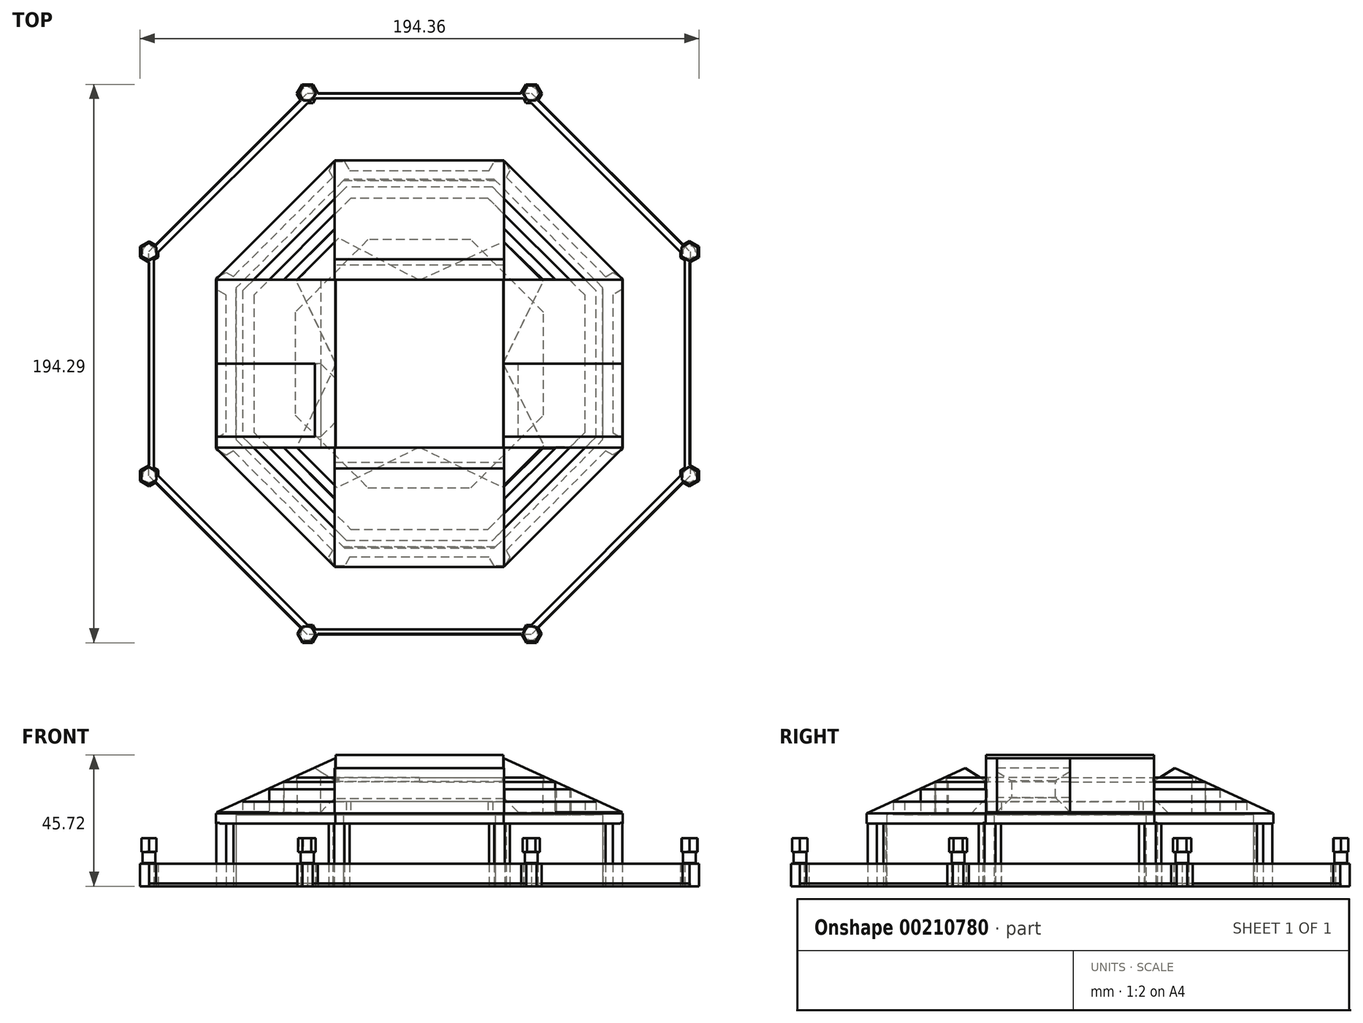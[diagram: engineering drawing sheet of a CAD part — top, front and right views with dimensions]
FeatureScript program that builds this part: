
annotation { "Feature Type Name" : "Feature", "Feature Type Description" : "" }
export const myFeature = defineFeature(function(context is Context, id is Id, definition is map)
    precondition{}
    {
        {
            var Q0;
            Q0=qCreatedBy(makeId("Top.planeOp"),FACE);
            cPlane(context, id + "F0", {"entities" : qUnion([Q0]), "cplaneType" : CPlaneType.OFFSET, "offset" : 31.24 * mm, "width" : 152.4 * mm, "height" : 152.4 * mm});
        }
        {
            var Q0;
            Q0=qCreatedBy(id+"F0.planeOp",FACE);
            cPlane(context, id + "F1", {"entities" : qUnion([Q0]), "cplaneType" : CPlaneType.OFFSET, "offset" : 19.05 * mm, "width" : 152.4 * mm, "height" : 152.4 * mm});
        }
        {
            var Q0;
            Q0=qCreatedBy(id+"F1.planeOp",FACE);
            cPlane(context, id + "F2", {"entities" : qUnion([Q0]), "cplaneType" : CPlaneType.OFFSET, "offset" : 25.4 * mm, "width" : 152.4 * mm, "height" : 152.4 * mm});
        }
        {
            var Q0;
            Q0=qCreatedBy(id+"F2.planeOp",FACE);
            cPlane(context, id + "F3", {"entities" : qUnion([Q0]), "cplaneType" : CPlaneType.OFFSET, "offset" : 6.35 * mm, "width" : 152.4 * mm, "height" : 152.4 * mm});
        }
        {
            var Q0;
            Q0=qCreatedBy(id+"F3.planeOp",FACE);
            cPlane(context, id + "F4", {"entities" : qUnion([Q0]), "cplaneType" : CPlaneType.OFFSET, "offset" : 17.78 * mm, "width" : 152.4 * mm, "height" : 152.4 * mm});
        }
        {
            var Q0;
            Q0=qCreatedBy(id+"F4.planeOp",FACE);
            cPlane(context, id + "F5", {"entities" : qUnion([Q0]), "cplaneType" : CPlaneType.OFFSET, "offset" : 3.3 * mm, "width" : 152.4 * mm, "height" : 152.4 * mm});
        }
        {
            var Q0;
            Q0=qCreatedBy(id+"F5.planeOp",FACE);
            cPlane(context, id + "F6", {"entities" : qUnion([Q0]), "cplaneType" : CPlaneType.OFFSET, "offset" : 34.8 * mm, "width" : 152.4 * mm, "height" : 152.4 * mm});
        }
        {
            var Q0;
            Q0=qCreatedBy(id+"F6.planeOp",FACE);
            var sketch = newSketch(context, id + "F7", { "sketchPlane" : qUnion([Q0])});
            skCircle(sketch, "E0.cCircle", {"center": v(0, 0) * mm, "radius": 94.16 * mm, "construction": true});
            skLineSegment(sketch, "E0.0", {"start": v(94.16, 39) * mm, "end": v(94.16, -39) * mm});
            skLineSegment(sketch, "E0.1", {"start": v(94.16, -39) * mm, "end": v(39, -94.16) * mm});
            skLineSegment(sketch, "E0.2", {"start": v(39, -94.16) * mm, "end": v(-39, -94.16) * mm});
            skLineSegment(sketch, "E0.3", {"start": v(-39, -94.16) * mm, "end": v(-94.16, -39) * mm});
            skLineSegment(sketch, "E0.4", {"start": v(-94.16, -39) * mm, "end": v(-94.16, 39) * mm});
            skLineSegment(sketch, "E0.5", {"start": v(-94.16, 39) * mm, "end": v(-39, 94.16) * mm});
            skLineSegment(sketch, "E0.6", {"start": v(-39, 94.16) * mm, "end": v(39, 94.16) * mm});
            skLineSegment(sketch, "E0.7", {"start": v(39, 94.16) * mm, "end": v(94.16, 39) * mm});
            skPoint(sketch, "E0.0.midPoint", {"position": v(94.16, 0) * mm});
            skCircle(sketch, "E1.cCircle", {"center": v(0, 0) * mm, "radius": 55.27 * mm, "construction": true});
            skLineSegment(sketch, "E1.0", {"start": v(-22.9, 55.27) * mm, "end": v(22.9, 55.27) * mm});
            skLineSegment(sketch, "E1.1", {"start": v(22.9, 55.27) * mm, "end": v(55.27, 22.9) * mm});
            skLineSegment(sketch, "E1.2", {"start": v(55.27, 22.9) * mm, "end": v(55.27, -22.9) * mm});
            skLineSegment(sketch, "E1.3", {"start": v(55.27, -22.9) * mm, "end": v(22.9, -55.27) * mm});
            skLineSegment(sketch, "E1.4", {"start": v(22.9, -55.27) * mm, "end": v(-22.9, -55.27) * mm});
            skLineSegment(sketch, "E1.5", {"start": v(-22.9, -55.27) * mm, "end": v(-55.27, -22.9) * mm});
            skLineSegment(sketch, "E1.6", {"start": v(-55.27, -22.9) * mm, "end": v(-55.27, 22.9) * mm});
            skLineSegment(sketch, "E1.7", {"start": v(-55.27, 22.9) * mm, "end": v(-22.9, 55.27) * mm});
            skPoint(sketch, "E1.0.midPoint", {"position": v(0, 55.27) * mm});
            skSolve(sketch);
        }
        {
            var Q0;
            Q0=qSketchRegion(id+"F7",true);
            extrude(context, id + "F8", {"entities" : qUnion([Q0]), "depth" : 1.02 * mm});
        }
        {
            var Q0;
            Q0=qCreatedBy(id+"F6.planeOp",FACE);
            var sketch = newSketch(context, id + "F9", { "sketchPlane" : qUnion([Q0])});
            skLineSegment(sketch, "E2.0", {"start": v(-38.92, 93.97) * mm, "end": v(38.92, 93.97) * mm});
            skLineSegment(sketch, "E2.1", {"start": v(38.92, 93.97) * mm, "end": v(93.97, 38.92) * mm});
            skLineSegment(sketch, "E2.2", {"start": v(93.97, 38.92) * mm, "end": v(93.97, -38.92) * mm});
            skLineSegment(sketch, "E2.3", {"start": v(93.97, -38.92) * mm, "end": v(38.92, -93.97) * mm});
            skLineSegment(sketch, "E2.4", {"start": v(38.92, -93.97) * mm, "end": v(-38.92, -93.97) * mm});
            skLineSegment(sketch, "E2.5", {"start": v(-38.92, -93.97) * mm, "end": v(-93.97, -38.92) * mm});
            skLineSegment(sketch, "E2.6", {"start": v(-93.97, -38.92) * mm, "end": v(-93.97, 38.92) * mm});
            skLineSegment(sketch, "E2.7", {"start": v(-93.97, 38.92) * mm, "end": v(-38.92, 93.97) * mm});
            skPoint(sketch, "E2.0.midPoint", {"position": v(0, 93.97) * mm});
            skCircle(sketch, "E3.cCircle", {"center": v(-38.92, -93.97) * mm, "radius": 3.1 * mm, "construction": true});
            skLineSegment(sketch, "E3.0", {"start": v(-40.71, -90.87) * mm, "end": v(-37.13, -90.87) * mm});
            skLineSegment(sketch, "E3.1", {"start": v(-37.13, -90.87) * mm, "end": v(-35.34, -93.97) * mm});
            skLineSegment(sketch, "E3.2", {"start": v(-35.34, -93.97) * mm, "end": v(-37.13, -97.07) * mm});
            skLineSegment(sketch, "E3.3", {"start": v(-37.13, -97.07) * mm, "end": v(-40.71, -97.07) * mm});
            skLineSegment(sketch, "E3.4", {"start": v(-40.71, -97.07) * mm, "end": v(-42.5, -93.97) * mm});
            skLineSegment(sketch, "E3.5", {"start": v(-42.5, -93.97) * mm, "end": v(-40.71, -90.87) * mm});
            skPoint(sketch, "E3.0.midPoint", {"position": v(-38.92, -90.87) * mm});
            skCircle(sketch, "E4.cCircle", {"center": v(38.92, -93.97) * mm, "radius": 3.1 * mm, "construction": true});
            skLineSegment(sketch, "E4.0", {"start": v(37.13, -90.87) * mm, "end": v(40.71, -90.87) * mm});
            skLineSegment(sketch, "E4.1", {"start": v(40.71, -90.87) * mm, "end": v(42.5, -93.97) * mm});
            skLineSegment(sketch, "E4.2", {"start": v(42.5, -93.97) * mm, "end": v(40.71, -97.07) * mm});
            skLineSegment(sketch, "E4.3", {"start": v(40.71, -97.07) * mm, "end": v(37.13, -97.07) * mm});
            skLineSegment(sketch, "E4.4", {"start": v(37.13, -97.07) * mm, "end": v(35.34, -93.97) * mm});
            skLineSegment(sketch, "E4.5", {"start": v(35.34, -93.97) * mm, "end": v(37.13, -90.87) * mm});
            skPoint(sketch, "E4.0.midPoint", {"position": v(38.92, -90.87) * mm});
            skCircle(sketch, "E5.cCircle", {"center": v(93.97, -38.92) * mm, "radius": 3.25 * mm, "construction": true});
            skLineSegment(sketch, "E5.0", {"start": v(90.72, -40.8) * mm, "end": v(90.72, -37.05) * mm});
            skLineSegment(sketch, "E5.1", {"start": v(90.72, -37.05) * mm, "end": v(93.97, -35.17) * mm});
            skLineSegment(sketch, "E5.2", {"start": v(93.97, -35.17) * mm, "end": v(97.22, -37.05) * mm});
            skLineSegment(sketch, "E5.3", {"start": v(97.22, -37.05) * mm, "end": v(97.22, -40.8) * mm});
            skLineSegment(sketch, "E5.4", {"start": v(97.22, -40.8) * mm, "end": v(93.97, -42.68) * mm});
            skLineSegment(sketch, "E5.5", {"start": v(93.97, -42.68) * mm, "end": v(90.72, -40.8) * mm});
            skPoint(sketch, "E5.0.midPoint", {"position": v(90.72, -38.92) * mm});
            skCircle(sketch, "E6.cCircle", {"center": v(93.97, 38.92) * mm, "radius": 3.25 * mm, "construction": true});
            skLineSegment(sketch, "E6.0", {"start": v(90.72, 37.05) * mm, "end": v(90.72, 40.8) * mm});
            skLineSegment(sketch, "E6.1", {"start": v(90.72, 40.8) * mm, "end": v(93.97, 42.68) * mm});
            skLineSegment(sketch, "E6.2", {"start": v(93.97, 42.68) * mm, "end": v(97.22, 40.8) * mm});
            skLineSegment(sketch, "E6.3", {"start": v(97.22, 40.8) * mm, "end": v(97.22, 37.05) * mm});
            skLineSegment(sketch, "E6.4", {"start": v(97.22, 37.05) * mm, "end": v(93.97, 35.17) * mm});
            skLineSegment(sketch, "E6.5", {"start": v(93.97, 35.17) * mm, "end": v(90.72, 37.05) * mm});
            skPoint(sketch, "E6.0.midPoint", {"position": v(90.72, 38.92) * mm});
            skCircle(sketch, "E7.cCircle", {"center": v(-93.97, -38.92) * mm, "radius": 3.17 * mm, "construction": true});
            skLineSegment(sketch, "E7.0", {"start": v(-90.8, -37.1) * mm, "end": v(-90.8, -40.76) * mm});
            skLineSegment(sketch, "E7.1", {"start": v(-90.8, -40.76) * mm, "end": v(-93.97, -42.59) * mm});
            skLineSegment(sketch, "E7.2", {"start": v(-93.97, -42.59) * mm, "end": v(-97.14, -40.76) * mm});
            skLineSegment(sketch, "E7.3", {"start": v(-97.14, -40.76) * mm, "end": v(-97.14, -37.1) * mm});
            skLineSegment(sketch, "E7.4", {"start": v(-97.14, -37.1) * mm, "end": v(-93.97, -35.26) * mm});
            skLineSegment(sketch, "E7.5", {"start": v(-93.97, -35.26) * mm, "end": v(-90.8, -37.1) * mm});
            skPoint(sketch, "E7.0.midPoint", {"position": v(-90.8, -38.92) * mm});
            skCircle(sketch, "E8.cCircle", {"center": v(-93.97, 38.92) * mm, "radius": 3.17 * mm, "construction": true});
            skLineSegment(sketch, "E8.0", {"start": v(-90.8, 40.76) * mm, "end": v(-90.8, 37.1) * mm});
            skLineSegment(sketch, "E8.1", {"start": v(-90.8, 37.1) * mm, "end": v(-93.97, 35.26) * mm});
            skLineSegment(sketch, "E8.2", {"start": v(-93.97, 35.26) * mm, "end": v(-97.14, 37.1) * mm});
            skLineSegment(sketch, "E8.3", {"start": v(-97.14, 37.1) * mm, "end": v(-97.14, 40.76) * mm});
            skLineSegment(sketch, "E8.4", {"start": v(-97.14, 40.76) * mm, "end": v(-93.97, 42.59) * mm});
            skLineSegment(sketch, "E8.5", {"start": v(-93.97, 42.59) * mm, "end": v(-90.8, 40.76) * mm});
            skPoint(sketch, "E8.0.midPoint", {"position": v(-90.8, 38.92) * mm});
            skCircle(sketch, "E9.cCircle", {"center": v(-38.92, 93.97) * mm, "radius": 3.25 * mm, "construction": true});
            skLineSegment(sketch, "E9.0", {"start": v(-37.05, 90.72) * mm, "end": v(-40.8, 90.72) * mm});
            skLineSegment(sketch, "E9.1", {"start": v(-40.8, 90.72) * mm, "end": v(-42.67, 93.97) * mm});
            skLineSegment(sketch, "E9.2", {"start": v(-42.67, 93.97) * mm, "end": v(-40.8, 97.22) * mm});
            skLineSegment(sketch, "E9.3", {"start": v(-40.8, 97.22) * mm, "end": v(-37.05, 97.22) * mm});
            skLineSegment(sketch, "E9.4", {"start": v(-37.05, 97.22) * mm, "end": v(-35.18, 93.97) * mm});
            skLineSegment(sketch, "E9.5", {"start": v(-35.18, 93.97) * mm, "end": v(-37.05, 90.72) * mm});
            skPoint(sketch, "E9.0.midPoint", {"position": v(-38.92, 90.72) * mm});
            skCircle(sketch, "E10.cCircle", {"center": v(38.92, 93.97) * mm, "radius": 3.25 * mm, "construction": true});
            skLineSegment(sketch, "E10.0", {"start": v(40.8, 90.72) * mm, "end": v(37.05, 90.72) * mm});
            skLineSegment(sketch, "E10.1", {"start": v(37.05, 90.72) * mm, "end": v(35.18, 93.97) * mm});
            skLineSegment(sketch, "E10.2", {"start": v(35.18, 93.97) * mm, "end": v(37.05, 97.22) * mm});
            skLineSegment(sketch, "E10.3", {"start": v(37.05, 97.22) * mm, "end": v(40.8, 97.22) * mm});
            skLineSegment(sketch, "E10.4", {"start": v(40.8, 97.22) * mm, "end": v(42.67, 93.97) * mm});
            skLineSegment(sketch, "E10.5", {"start": v(42.67, 93.97) * mm, "end": v(40.8, 90.72) * mm});
            skPoint(sketch, "E10.0.midPoint", {"position": v(38.92, 90.72) * mm});
            skLineSegment(sketch, "E11", {"start": v(-36.24, -92.42) * mm, "end": v(36.24, -92.42) * mm});
            skLineSegment(sketch, "E12", {"start": v(92.34, -36.1) * mm, "end": v(92.34, 36.1) * mm});
            skLineSegment(sketch, "E13", {"start": v(36.11, 92.35) * mm, "end": v(-36.11, 92.35) * mm});
            skLineSegment(sketch, "E14", {"start": v(-92.38, 36.17) * mm, "end": v(-92.38, -36.17) * mm});
            skLineSegment(sketch, "E15", {"start": v(38.92, -90.87) * mm, "end": v(90.72, -38.92) * mm});
            skLineSegment(sketch, "E16", {"start": v(90.72, 38.92) * mm, "end": v(38.92, 90.72) * mm});
            skLineSegment(sketch, "E17", {"start": v(-38.92, 90.72) * mm, "end": v(-90.8, 38.92) * mm});
            skLineSegment(sketch, "E18", {"start": v(-90.8, -38.92) * mm, "end": v(-38.92, -90.87) * mm});
            skSolve(sketch);
        }
        {
            var Q0;
            Q0=qSketchRegion(id+"F9",true);
            extrude(context, id + "F10", {"entities" : qUnion([Q0]), "depth" : 7.87 * mm});
        }
        {
            var Q0;
            Q0=qCreatedBy(id+"F6.planeOp",FACE);
            var sketch = newSketch(context, id + "F11", { "sketchPlane" : qUnion([Q0])});
            skLineSegment(sketch, "E19.0", {"start": v(-67.24, -27.85) * mm, "end": v(-67.24, 27.85) * mm});
            skLineSegment(sketch, "E19.1", {"start": v(-67.24, 27.85) * mm, "end": v(-27.85, 67.24) * mm});
            skLineSegment(sketch, "E19.2", {"start": v(-27.85, 67.24) * mm, "end": v(27.85, 67.24) * mm});
            skLineSegment(sketch, "E19.3", {"start": v(27.85, 67.24) * mm, "end": v(67.24, 27.85) * mm});
            skLineSegment(sketch, "E19.4", {"start": v(67.24, 27.85) * mm, "end": v(67.24, -27.85) * mm});
            skLineSegment(sketch, "E19.5", {"start": v(67.24, -27.85) * mm, "end": v(27.85, -67.24) * mm});
            skLineSegment(sketch, "E19.6", {"start": v(27.85, -67.24) * mm, "end": v(-27.85, -67.24) * mm});
            skLineSegment(sketch, "E19.7", {"start": v(-27.85, -67.24) * mm, "end": v(-67.24, -27.85) * mm});
            skPoint(sketch, "E19.0.midPoint", {"position": v(-67.24, 0) * mm});
            skCircle(sketch, "E20.cCircle", {"center": v(67.24, -27.85) * mm, "radius": 3.35 * mm, "construction": true});
            skLineSegment(sketch, "E20.0", {"start": v(70.59, -25.92) * mm, "end": v(70.59, -29.78) * mm});
            skLineSegment(sketch, "E20.1", {"start": v(70.59, -29.78) * mm, "end": v(67.24, -31.72) * mm});
            skLineSegment(sketch, "E20.2", {"start": v(67.24, -31.72) * mm, "end": v(63.89, -29.78) * mm});
            skLineSegment(sketch, "E20.3", {"start": v(63.89, -29.78) * mm, "end": v(63.89, -25.92) * mm});
            skLineSegment(sketch, "E20.4", {"start": v(63.89, -25.92) * mm, "end": v(67.24, -23.98) * mm});
            skLineSegment(sketch, "E20.5", {"start": v(67.24, -23.98) * mm, "end": v(70.59, -25.92) * mm});
            skPoint(sketch, "E20.0.midPoint", {"position": v(70.59, -27.85) * mm});
            skCircle(sketch, "E21.cCircle", {"center": v(67.24, 27.85) * mm, "radius": 3.35 * mm, "construction": true});
            skLineSegment(sketch, "E21.0", {"start": v(70.59, 29.78) * mm, "end": v(70.59, 25.92) * mm});
            skLineSegment(sketch, "E21.1", {"start": v(70.59, 25.92) * mm, "end": v(67.24, 23.98) * mm});
            skLineSegment(sketch, "E21.2", {"start": v(67.24, 23.98) * mm, "end": v(63.89, 25.92) * mm});
            skLineSegment(sketch, "E21.3", {"start": v(63.89, 25.92) * mm, "end": v(63.89, 29.78) * mm});
            skLineSegment(sketch, "E21.4", {"start": v(63.89, 29.78) * mm, "end": v(67.24, 31.72) * mm});
            skLineSegment(sketch, "E21.5", {"start": v(67.24, 31.72) * mm, "end": v(70.59, 29.78) * mm});
            skPoint(sketch, "E21.0.midPoint", {"position": v(70.59, 27.85) * mm});
            skCircle(sketch, "E22.cCircle", {"center": v(27.85, 67.24) * mm, "radius": 3.12 * mm, "construction": true});
            skLineSegment(sketch, "E22.0", {"start": v(26.05, 70.36) * mm, "end": v(29.65, 70.36) * mm});
            skLineSegment(sketch, "E22.1", {"start": v(29.65, 70.36) * mm, "end": v(31.46, 67.24) * mm});
            skLineSegment(sketch, "E22.2", {"start": v(31.46, 67.24) * mm, "end": v(29.65, 64.11) * mm});
            skLineSegment(sketch, "E22.3", {"start": v(29.65, 64.11) * mm, "end": v(26.05, 64.11) * mm});
            skLineSegment(sketch, "E22.4", {"start": v(26.05, 64.11) * mm, "end": v(24.24, 67.24) * mm});
            skLineSegment(sketch, "E22.5", {"start": v(24.24, 67.24) * mm, "end": v(26.05, 70.36) * mm});
            skPoint(sketch, "E22.0.midPoint", {"position": v(27.85, 70.36) * mm});
            skCircle(sketch, "E23.cCircle", {"center": v(-27.85, 67.24) * mm, "radius": 3.12 * mm, "construction": true});
            skLineSegment(sketch, "E23.0", {"start": v(-29.65, 70.36) * mm, "end": v(-26.05, 70.36) * mm});
            skLineSegment(sketch, "E23.1", {"start": v(-26.05, 70.36) * mm, "end": v(-24.24, 67.24) * mm});
            skLineSegment(sketch, "E23.2", {"start": v(-24.24, 67.24) * mm, "end": v(-26.05, 64.11) * mm});
            skLineSegment(sketch, "E23.3", {"start": v(-26.05, 64.11) * mm, "end": v(-29.65, 64.11) * mm});
            skLineSegment(sketch, "E23.4", {"start": v(-29.65, 64.11) * mm, "end": v(-31.46, 67.24) * mm});
            skLineSegment(sketch, "E23.5", {"start": v(-31.46, 67.24) * mm, "end": v(-29.65, 70.36) * mm});
            skPoint(sketch, "E23.0.midPoint", {"position": v(-27.85, 70.36) * mm});
            skCircle(sketch, "E24.cCircle", {"center": v(27.85, -67.24) * mm, "radius": 3.13 * mm, "construction": true});
            skLineSegment(sketch, "E24.0", {"start": v(29.66, -70.37) * mm, "end": v(26.04, -70.37) * mm});
            skLineSegment(sketch, "E24.1", {"start": v(26.04, -70.37) * mm, "end": v(24.23, -67.24) * mm});
            skLineSegment(sketch, "E24.2", {"start": v(24.23, -67.24) * mm, "end": v(26.04, -64.1) * mm});
            skLineSegment(sketch, "E24.3", {"start": v(26.04, -64.1) * mm, "end": v(29.66, -64.1) * mm});
            skLineSegment(sketch, "E24.4", {"start": v(29.66, -64.1) * mm, "end": v(31.47, -67.24) * mm});
            skLineSegment(sketch, "E24.5", {"start": v(31.47, -67.24) * mm, "end": v(29.66, -70.37) * mm});
            skPoint(sketch, "E24.0.midPoint", {"position": v(27.85, -70.37) * mm});
            skCircle(sketch, "E25.cCircle", {"center": v(-27.85, -67.24) * mm, "radius": 3.13 * mm, "construction": true});
            skLineSegment(sketch, "E25.0", {"start": v(-26.04, -70.37) * mm, "end": v(-29.66, -70.37) * mm});
            skLineSegment(sketch, "E25.1", {"start": v(-29.66, -70.37) * mm, "end": v(-31.47, -67.24) * mm});
            skLineSegment(sketch, "E25.2", {"start": v(-31.47, -67.24) * mm, "end": v(-29.66, -64.1) * mm});
            skLineSegment(sketch, "E25.3", {"start": v(-29.66, -64.1) * mm, "end": v(-26.04, -64.1) * mm});
            skLineSegment(sketch, "E25.4", {"start": v(-26.04, -64.1) * mm, "end": v(-24.23, -67.24) * mm});
            skLineSegment(sketch, "E25.5", {"start": v(-24.23, -67.24) * mm, "end": v(-26.04, -70.37) * mm});
            skPoint(sketch, "E25.0.midPoint", {"position": v(-27.85, -70.37) * mm});
            skCircle(sketch, "E26.cCircle", {"center": v(-67.24, -27.85) * mm, "radius": 3.44 * mm, "construction": true});
            skLineSegment(sketch, "E26.0", {"start": v(-70.68, -29.84) * mm, "end": v(-70.68, -25.86) * mm});
            skLineSegment(sketch, "E26.1", {"start": v(-70.68, -25.86) * mm, "end": v(-67.24, -23.88) * mm});
            skLineSegment(sketch, "E26.2", {"start": v(-67.24, -23.88) * mm, "end": v(-63.8, -25.86) * mm});
            skLineSegment(sketch, "E26.3", {"start": v(-63.8, -25.86) * mm, "end": v(-63.8, -29.84) * mm});
            skLineSegment(sketch, "E26.4", {"start": v(-63.8, -29.84) * mm, "end": v(-67.24, -31.82) * mm});
            skLineSegment(sketch, "E26.5", {"start": v(-67.24, -31.82) * mm, "end": v(-70.68, -29.84) * mm});
            skPoint(sketch, "E26.0.midPoint", {"position": v(-70.68, -27.85) * mm});
            skCircle(sketch, "E27.cCircle", {"center": v(-67.24, 27.85) * mm, "radius": 3.44 * mm, "construction": true});
            skLineSegment(sketch, "E27.0", {"start": v(-70.68, 25.86) * mm, "end": v(-70.68, 29.84) * mm});
            skLineSegment(sketch, "E27.1", {"start": v(-70.68, 29.84) * mm, "end": v(-67.24, 31.82) * mm});
            skLineSegment(sketch, "E27.2", {"start": v(-67.24, 31.82) * mm, "end": v(-63.8, 29.84) * mm});
            skLineSegment(sketch, "E27.3", {"start": v(-63.8, 29.84) * mm, "end": v(-63.8, 25.86) * mm});
            skLineSegment(sketch, "E27.4", {"start": v(-63.8, 25.86) * mm, "end": v(-67.24, 23.88) * mm});
            skLineSegment(sketch, "E27.5", {"start": v(-67.24, 23.88) * mm, "end": v(-70.68, 25.86) * mm});
            skPoint(sketch, "E27.0.midPoint", {"position": v(-70.68, 27.85) * mm});
            skLineSegment(sketch, "E28", {"start": v(-26.04, -64.1) * mm, "end": v(26.04, -64.1) * mm});
            skLineSegment(sketch, "E29", {"start": v(26.04, -64.1) * mm, "end": v(63.89, -25.92) * mm});
            skLineSegment(sketch, "E30", {"start": v(63.89, -25.92) * mm, "end": v(63.89, 25.92) * mm});
            skLineSegment(sketch, "E31", {"start": v(63.89, 25.92) * mm, "end": v(26.05, 64.11) * mm});
            skLineSegment(sketch, "E32", {"start": v(26.05, 64.11) * mm, "end": v(-26.05, 64.11) * mm});
            skLineSegment(sketch, "E33", {"start": v(-26.05, 64.11) * mm, "end": v(-63.8, 25.86) * mm});
            skLineSegment(sketch, "E34", {"start": v(-63.8, 25.86) * mm, "end": v(-63.8, -25.86) * mm});
            skLineSegment(sketch, "E35", {"start": v(-63.8, -25.86) * mm, "end": v(-26.04, -64.1) * mm});
            skSolve(sketch);
        }
        {
            var Q0;
            Q0=qSketchRegion(id+"F11",true);
            extrude(context, id + "F12", {"entities" : qUnion([Q0]), "depth" : 22.1 * mm});
        }
        {
            var Q0;
            Q0=qCreatedBy(id+"F6.planeOp",FACE);
            cPlane(context, id + "F13", {"entities" : qUnion([Q0]), "cplaneType" : CPlaneType.OFFSET, "offset" : 21.84 * mm, "width" : 152.4 * mm, "height" : 152.4 * mm});
        }
        {
            var Q0;
            Q0=qCreatedBy(id+"F13.planeOp",FACE);
            var sketch = newSketch(context, id + "F14", { "sketchPlane" : qUnion([Q0])});
            skCircle(sketch, "E36.cCircle", {"center": v(0, 0) * mm, "radius": 70.74 * mm, "construction": true});
            skLineSegment(sketch, "E36.0", {"start": v(29.3, -70.74) * mm, "end": v(-29.3, -70.74) * mm});
            skLineSegment(sketch, "E36.1", {"start": v(-29.3, -70.74) * mm, "end": v(-70.74, -29.3) * mm});
            skLineSegment(sketch, "E36.2", {"start": v(-70.74, -29.3) * mm, "end": v(-70.74, 29.3) * mm});
            skLineSegment(sketch, "E36.3", {"start": v(-70.74, 29.3) * mm, "end": v(-29.3, 70.74) * mm});
            skLineSegment(sketch, "E36.4", {"start": v(-29.3, 70.74) * mm, "end": v(29.3, 70.74) * mm});
            skLineSegment(sketch, "E36.5", {"start": v(29.3, 70.74) * mm, "end": v(70.74, 29.3) * mm});
            skLineSegment(sketch, "E36.6", {"start": v(70.74, 29.3) * mm, "end": v(70.74, -29.3) * mm});
            skLineSegment(sketch, "E36.7", {"start": v(70.74, -29.3) * mm, "end": v(29.3, -70.74) * mm});
            skPoint(sketch, "E36.0.midPoint", {"position": v(0, -70.74) * mm});
            skCircle(sketch, "E37.cCircle", {"center": v(0, 0) * mm, "radius": 43.18 * mm, "construction": true});
            skLineSegment(sketch, "E37.0", {"start": v(17.89, -43.18) * mm, "end": v(-17.89, -43.18) * mm});
            skLineSegment(sketch, "E37.1", {"start": v(-17.89, -43.18) * mm, "end": v(-43.18, -17.89) * mm});
            skLineSegment(sketch, "E37.2", {"start": v(-43.18, -17.89) * mm, "end": v(-43.18, 17.89) * mm});
            skLineSegment(sketch, "E37.3", {"start": v(-43.18, 17.89) * mm, "end": v(-17.89, 43.18) * mm});
            skLineSegment(sketch, "E37.4", {"start": v(-17.89, 43.18) * mm, "end": v(17.89, 43.18) * mm});
            skLineSegment(sketch, "E37.5", {"start": v(17.89, 43.18) * mm, "end": v(43.18, 17.89) * mm});
            skLineSegment(sketch, "E37.6", {"start": v(43.18, 17.89) * mm, "end": v(43.18, -17.89) * mm});
            skLineSegment(sketch, "E37.7", {"start": v(43.18, -17.89) * mm, "end": v(17.89, -43.18) * mm});
            skPoint(sketch, "E37.0.midPoint", {"position": v(0, -43.18) * mm});
            skSolve(sketch);
        }
        {
            var Q0;
            Q0=qSketchRegion(id+"F14",true);
            extrude(context, id + "F15", {"entities" : qUnion([Q0]), "operationType" : NewBodyOperationType.ADD, "depth" : 3.56 * mm});
        }
        {
            var Q0;
            Q0=qCreatedBy(makeId("Front.planeOp"),FACE);
            var sketch = newSketch(context, id + "F16", { "sketchPlane" : qUnion([Q0])});
            skPoint(sketch, "E38.0.midPoint", {"position": v(0, 189.03) * mm});
            skLineSegment(sketch, "E39.left", {"start": v(-70.52, 163.7) * mm, "end": v(-70.52, 163.7) * mm});
            skLineSegment(sketch, "E39.right", {"start": v(70.52, 163.7) * mm, "end": v(70.52, 163.7) * mm});
            skPoint(sketch, "E39.middle", {"position": v(0, 163.7) * mm});
            skLineSegment(sketch, "E40", {"start": v(-29.24, 163.7) * mm, "end": v(-29.24, 182.4) * mm});
            skLineSegment(sketch, "E41", {"start": v(-29.24, 182.4) * mm, "end": v(-70.52, 163.7) * mm});
            skLineSegment(sketch, "E42", {"start": v(29.24, 182.4) * mm, "end": v(70.52, 163.7) * mm});
            skLineSegment(sketch, "E43", {"start": v(29.24, 182.4) * mm, "end": v(29.24, 163.7) * mm});
            skLineSegment(sketch, "E44", {"start": v(29.24, 163.7) * mm, "end": v(70.52, 163.7) * mm});
            skLineSegment(sketch, "E45", {"start": v(-70.52, 163.7) * mm, "end": v(-29.24, 163.7) * mm});
            skSolve(sketch);
        }
        {
            var Q0;
            Q0=qSketchRegion(id+"F16",true);
            extrude(context, id + "F17", {"entities" : qUnion([Q0]), "endBound" : BoundingType.SYMMETRIC, "depth" : 58.42 * mm});
        }
        {
            var Q0;
            Q0=qCreatedBy(makeId("Right.planeOp"),FACE);
            var sketch = newSketch(context, id + "F18", { "sketchPlane" : qUnion([Q0])});
            skPoint(sketch, "E46.0.midPoint", {"position": v(0, 188.96) * mm});
            skLineSegment(sketch, "E47.bottom", {"start": v(70.71, 163.3) * mm, "end": v(-70.71, 163.3) * mm});
            skLineSegment(sketch, "E47.top", {"start": v(70.71, 163.3) * mm, "end": v(-70.71, 163.3) * mm});
            skLineSegment(sketch, "E47.left", {"start": v(70.71, 163.3) * mm, "end": v(70.71, 163.3) * mm});
            skLineSegment(sketch, "E47.right", {"start": v(-70.71, 163.3) * mm, "end": v(-70.71, 163.3) * mm});
            skPoint(sketch, "E47.middle", {"position": v(0, 163.3) * mm});
            skLineSegment(sketch, "E48", {"start": v(-29.2, 182.35) * mm, "end": v(-29.2, 163.3) * mm});
            skLineSegment(sketch, "E49", {"start": v(29.2, 182.35) * mm, "end": v(29.2, 163.3) * mm});
            skLineSegment(sketch, "E50", {"start": v(-70.71, 163.3) * mm, "end": v(-29.2, 163.3) * mm});
            skLineSegment(sketch, "E51", {"start": v(-70.71, 163.3) * mm, "end": v(-29.2, 182.35) * mm});
            skLineSegment(sketch, "E52", {"start": v(29.2, 182.35) * mm, "end": v(70.71, 163.3) * mm});
            skSolve(sketch);
        }
        {
            var Q0;
            Q0=qSketchRegion(id+"F18",true);
            extrude(context, id + "F19", {"entities" : qUnion([Q0]), "endBound" : BoundingType.SYMMETRIC, "depth" : 58.93 * mm});
        }
        {
            var Q0;
            Q0=qSketchRegion(id+"F16",true);
            extrude(context, id + "F20", {"entities" : qUnion([Q0]), "depth" : 25.4 * mm});
        }
        {
            var Q0;
            Q0=qCreatedBy(id+"F13.planeOp",FACE);
            var sketch = newSketch(context, id + "F21", { "sketchPlane" : qUnion([Q0])});
            skCircle(sketch, "E53.cCircle", {"center": v(0, 0) * mm, "radius": 57.6 * mm, "construction": true});
            skLineSegment(sketch, "E53.0", {"start": v(57.6, 23.86) * mm, "end": v(57.6, -23.86) * mm});
            skLineSegment(sketch, "E53.1", {"start": v(57.6, -23.86) * mm, "end": v(23.86, -57.6) * mm});
            skLineSegment(sketch, "E53.2", {"start": v(23.86, -57.6) * mm, "end": v(-23.86, -57.6) * mm});
            skLineSegment(sketch, "E53.3", {"start": v(-23.86, -57.6) * mm, "end": v(-57.6, -23.86) * mm});
            skLineSegment(sketch, "E53.4", {"start": v(-57.6, -23.86) * mm, "end": v(-57.6, 23.86) * mm});
            skLineSegment(sketch, "E53.5", {"start": v(-57.6, 23.86) * mm, "end": v(-23.86, 57.6) * mm});
            skLineSegment(sketch, "E53.6", {"start": v(-23.86, 57.6) * mm, "end": v(23.86, 57.6) * mm});
            skLineSegment(sketch, "E53.7", {"start": v(23.86, 57.6) * mm, "end": v(57.6, 23.86) * mm});
            skPoint(sketch, "E53.0.midPoint", {"position": v(57.6, 0) * mm});
            skCircle(sketch, "E54.cCircle", {"center": v(0, 0) * mm, "radius": 61.43 * mm, "construction": true});
            skPoint(sketch, "E54.cCircle.perimeterSnap0", {"position": v(-57.6, 0) * mm});
            skLineSegment(sketch, "E54.0", {"start": v(-61.43, -25.45) * mm, "end": v(-61.43, 25.45) * mm});
            skLineSegment(sketch, "E54.1", {"start": v(-61.43, 25.45) * mm, "end": v(-25.45, 61.43) * mm});
            skLineSegment(sketch, "E54.2", {"start": v(-25.45, 61.43) * mm, "end": v(25.45, 61.43) * mm});
            skLineSegment(sketch, "E54.3", {"start": v(25.45, 61.43) * mm, "end": v(61.43, 25.45) * mm});
            skLineSegment(sketch, "E54.4", {"start": v(61.43, 25.45) * mm, "end": v(61.43, -25.45) * mm});
            skLineSegment(sketch, "E54.5", {"start": v(61.43, -25.45) * mm, "end": v(25.45, -61.43) * mm});
            skLineSegment(sketch, "E54.6", {"start": v(25.45, -61.43) * mm, "end": v(-25.45, -61.43) * mm});
            skLineSegment(sketch, "E54.7", {"start": v(-25.45, -61.43) * mm, "end": v(-61.43, -25.45) * mm});
            skPoint(sketch, "E54.0.midPoint", {"position": v(-61.43, 0) * mm});
            skPoint(sketch, "E54.0.midPoint.positionSnap0", {"position": v(-57.6, 0) * mm});
            skSolve(sketch);
        }
        {
            var Q0;
            Q0=qSketchRegion(id+"F21",true);
            extrude(context, id + "F22", {"entities" : qUnion([Q0]), "depth" : 7.62 * mm});
        }
        {
            var Q0;
            Q0=qCreatedBy(id+"F13.planeOp",FACE);
            var sketch = newSketch(context, id + "F23", { "sketchPlane" : qUnion([Q0])});
            skPoint(sketch, "E55.0.midPoint", {"position": v(-40.84, 40.66) * mm});
            skPoint(sketch, "E56.0.midPoint", {"position": v(0, 54.02) * mm});
            skLineSegment(sketch, "E57", {"start": v(52.63, -28.82) * mm, "end": v(47.58, -28.82) * mm});
            skLineSegment(sketch, "E58", {"start": v(29.57, -51.99) * mm, "end": v(29.57, -46.84) * mm});
            skLineSegment(sketch, "E59", {"start": v(52.3, 29.26) * mm, "end": v(47.14, 29.26) * mm});
            skLineSegment(sketch, "E60", {"start": v(47.14, 29.26) * mm, "end": v(52.3, 29.26) * mm});
            skLineSegment(sketch, "E61", {"start": v(29.46, 52) * mm, "end": v(29.46, 46.95) * mm});
            skLineSegment(sketch, "E62", {"start": v(-29.43, 46.97) * mm, "end": v(-29.43, 52.13) * mm});
            skLineSegment(sketch, "E63", {"start": v(-47.2, 29.2) * mm, "end": v(-52.24, 29.2) * mm});
            skLineSegment(sketch, "E64", {"start": v(-52.24, 29.2) * mm, "end": v(-47.2, 29.2) * mm});
            skLineSegment(sketch, "E65", {"start": v(-47.2, -29.2) * mm, "end": v(-52.24, -29.2) * mm});
            skLineSegment(sketch, "E66", {"start": v(-29.46, -46.94) * mm, "end": v(-29.46, -52) * mm});
            skLineSegment(sketch, "E67", {"start": v(-29.46, -52) * mm, "end": v(-29.46, -45.28) * mm});
            skLineSegment(sketch, "E68", {"start": v(29.57, -51.99) * mm, "end": v(52.63, -28.82) * mm});
            skLineSegment(sketch, "E69", {"start": v(47.58, -28.82) * mm, "end": v(29.57, -46.84) * mm});
            skLineSegment(sketch, "E70", {"start": v(47.14, 29.26) * mm, "end": v(29.46, 46.95) * mm});
            skLineSegment(sketch, "E71", {"start": v(52.3, 29.26) * mm, "end": v(29.46, 52) * mm});
            skLineSegment(sketch, "E72", {"start": v(29.46, 46.95) * mm, "end": v(47.14, 29.26) * mm});
            skLineSegment(sketch, "E73", {"start": v(-52.24, 29.2) * mm, "end": v(-29.43, 52.13) * mm});
            skLineSegment(sketch, "E74", {"start": v(-29.43, 46.97) * mm, "end": v(-47.2, 29.2) * mm});
            skLineSegment(sketch, "E75", {"start": v(-52.24, -29.2) * mm, "end": v(-29.46, -52) * mm});
            skLineSegment(sketch, "E76", {"start": v(-47.2, -29.2) * mm, "end": v(-29.46, -46.94) * mm});
            skSolve(sketch);
        }
        {
            var Q0;
            Q0=qSketchRegion(id+"F23",true);
            extrude(context, id + "F24", {"entities" : qUnion([Q0]), "depth" : 11.94 * mm});
        }
        {
            var Q0;
            Q0=qCreatedBy(id+"F13.planeOp",FACE);
            var sketch = newSketch(context, id + "F25", { "sketchPlane" : qUnion([Q0])});
            skLineSegment(sketch, "E77", {"start": v(-47.23, 29.16) * mm, "end": v(-29.4, 46.93) * mm});
            skLineSegment(sketch, "E78", {"start": v(-29.4, 46.93) * mm, "end": v(-29.4, 42.28) * mm});
            skLineSegment(sketch, "E79", {"start": v(-29.4, 42.28) * mm, "end": v(-42.6, 29.16) * mm});
            skLineSegment(sketch, "E80", {"start": v(-47.23, 29.16) * mm, "end": v(-42.6, 29.16) * mm});
            skLineSegment(sketch, "E81", {"start": v(-47.23, -29.1) * mm, "end": v(-42.6, -29.1) * mm});
            skLineSegment(sketch, "E82", {"start": v(-42.6, -29.1) * mm, "end": v(-29.4, -42.37) * mm});
            skLineSegment(sketch, "E83", {"start": v(-29.4, -42.37) * mm, "end": v(-29.4, -46.79) * mm});
            skLineSegment(sketch, "E84", {"start": v(-29.4, -46.79) * mm, "end": v(-47.23, -29.1) * mm});
            skLineSegment(sketch, "E85", {"start": v(29.45, 47.07) * mm, "end": v(47.17, 29.34) * mm});
            skLineSegment(sketch, "E86", {"start": v(29.45, 42.28) * mm, "end": v(42.87, 29.34) * mm});
            skLineSegment(sketch, "E87", {"start": v(29.45, 47.07) * mm, "end": v(29.45, 42.28) * mm});
            skLineSegment(sketch, "E88", {"start": v(42.87, 29.34) * mm, "end": v(47.17, 29.34) * mm});
            skLineSegment(sketch, "E89", {"start": v(47.17, -29.43) * mm, "end": v(29.45, -47.13) * mm});
            skLineSegment(sketch, "E90", {"start": v(42.87, -29.43) * mm, "end": v(29.45, -42.83) * mm});
            skLineSegment(sketch, "E91", {"start": v(42.87, -29.43) * mm, "end": v(47.17, -29.43) * mm});
            skLineSegment(sketch, "E92", {"start": v(29.45, -42.83) * mm, "end": v(29.45, -47.13) * mm});
            skSolve(sketch);
        }
        {
            var Q0;
            Q0=qSketchRegion(id+"F25",true);
            extrude(context, id + "F26", {"entities" : qUnion([Q0]), "depth" : 14.48 * mm});
        }
        {
            var Q0;
            Q0=qCreatedBy(id+"F13.planeOp",FACE);
            cPlane(context, id + "F27", {"entities" : qUnion([Q0]), "cplaneType" : CPlaneType.OFFSET, "offset" : 14.48 * mm, "width" : 152.4 * mm, "height" : 152.4 * mm});
        }
        {
            var Q0;
            Q0=qCreatedBy(id+"F27.planeOp",FACE);
            var sketch = newSketch(context, id + "F28", { "sketchPlane" : qUnion([Q0])});
            skPoint(sketch, "E93.0.midPoint", {"position": v(-35.87, 35.88) * mm});
            skPoint(sketch, "E94.0.midPoint", {"position": v(0, 29.06) * mm});
            skLineSegment(sketch, "E95", {"start": v(0, 29.06) * mm, "end": v(-28.05, 43.7) * mm});
            skLineSegment(sketch, "E96", {"start": v(0, 29.06) * mm, "end": v(29.23, 42.52) * mm});
            skLineSegment(sketch, "E97", {"start": v(29.06, 0) * mm, "end": v(43.03, 28.71) * mm});
            skLineSegment(sketch, "E98", {"start": v(-29.06, 0) * mm, "end": v(-42.84, 28.91) * mm});
            skLineSegment(sketch, "E99", {"start": v(-29.06, 0) * mm, "end": v(-42.7, -29.05) * mm});
            skLineSegment(sketch, "E100", {"start": v(0, -29.06) * mm, "end": v(-28.62, -43.13) * mm});
            skLineSegment(sketch, "E101", {"start": v(0, -29.06) * mm, "end": v(28.84, -42.9) * mm});
            skLineSegment(sketch, "E102", {"start": v(29.06, 0) * mm, "end": v(43.29, -28.46) * mm});
            skLineSegment(sketch, "E103", {"start": v(-42.7, -29.05) * mm, "end": v(-28.62, -43.13) * mm});
            skLineSegment(sketch, "E104", {"start": v(28.84, -42.9) * mm, "end": v(43.29, -28.46) * mm});
            skLineSegment(sketch, "E105", {"start": v(43.03, 28.71) * mm, "end": v(29.23, 42.52) * mm});
            skLineSegment(sketch, "E106", {"start": v(-28.05, 43.7) * mm, "end": v(-42.84, 28.91) * mm});
            skSolve(sketch);
        }
        {
            var Q0;
            Q0=qSketchRegion(id+"F28",true);
            extrude(context, id + "F29", {"entities" : qUnion([Q0]), "depth" : 1.52 * mm});
        }
        {
            var Q0;
            Q0=qCreatedBy(id+"F27.planeOp",FACE);
            cPlane(context, id + "F30", {"entities" : qUnion([Q0]), "cplaneType" : CPlaneType.OFFSET, "offset" : 1.52 * mm, "width" : 152.4 * mm, "height" : 152.4 * mm});
        }
        {
            var Q0;
            Q0=qCreatedBy(id+"F30.planeOp",FACE);
            var sketch = newSketch(context, id + "F31", { "sketchPlane" : qUnion([Q0])});
            skLineSegment(sketch, "E107.bottom", {"start": v(-29.15, 29.2) * mm, "end": v(29.15, 29.2) * mm});
            skLineSegment(sketch, "E107.top", {"start": v(-29.15, -29.2) * mm, "end": v(29.15, -29.2) * mm});
            skLineSegment(sketch, "E107.left", {"start": v(-29.15, 29.2) * mm, "end": v(-29.15, -29.2) * mm});
            skLineSegment(sketch, "E107.right", {"start": v(29.15, 29.2) * mm, "end": v(29.15, -29.2) * mm});
            skPoint(sketch, "E107.middle", {"position": v(0, 0) * mm});
            skSolve(sketch);
        }
        {
            var Q0;
            Q0=qSketchRegion(id+"F31",true);
            extrude(context, id + "F32", {"entities" : qUnion([Q0]), "depth" : 7.87 * mm});
        }
        {
            var Q0;
            Q0=makeQuery(id+"F8.opExtrude","CAP_FACE",FACE,{"disambiguationData":[OSD([sQuery(id+"F7.wireOp",EDGE,"E0.0"),sQuery(id+"F7.wireOp",EDGE,"E0.1"),sQuery(id+"F7.wireOp",EDGE,"E0.2"),sQuery(id+"F7.wireOp",EDGE,"E0.3"),sQuery(id+"F7.wireOp",EDGE,"E0.4"),sQuery(id+"F7.wireOp",EDGE,"E0.5"),sQuery(id+"F7.wireOp",EDGE,"E0.6"),sQuery(id+"F7.wireOp",EDGE,"E0.7"),sQuery(id+"F7.wireOp",EDGE,"E1.0"),sQuery(id+"F7.wireOp",EDGE,"E1.1"),sQuery(id+"F7.wireOp",EDGE,"E1.2"),sQuery(id+"F7.wireOp",EDGE,"E1.3"),sQuery(id+"F7.wireOp",EDGE,"E1.4"),sQuery(id+"F7.wireOp",EDGE,"E1.5"),sQuery(id+"F7.wireOp",EDGE,"E1.6"),sQuery(id+"F7.wireOp",EDGE,"E1.7")])],"isStart":true});
            var sketch = newSketch(context, id + "F33", { "sketchPlane" : qUnion([Q0])});
            skCircle(sketch, "E108.cCircle", {"center": v(0, 0) * mm, "radius": 63.77 * mm, "construction": true});
            skPoint(sketch, "E108.cCircle.perimeterSnap0", {"position": v(0, 55.27) * mm});
            skLineSegment(sketch, "E108.0", {"start": v(-26.41, 63.77) * mm, "end": v(26.41, 63.77) * mm});
            skLineSegment(sketch, "E108.1", {"start": v(26.41, 63.77) * mm, "end": v(63.77, 26.41) * mm});
            skLineSegment(sketch, "E108.2", {"start": v(63.77, 26.41) * mm, "end": v(63.77, -26.41) * mm});
            skLineSegment(sketch, "E108.3", {"start": v(63.77, -26.41) * mm, "end": v(26.41, -63.77) * mm});
            skLineSegment(sketch, "E108.4", {"start": v(26.41, -63.77) * mm, "end": v(-26.41, -63.77) * mm});
            skLineSegment(sketch, "E108.5", {"start": v(-26.41, -63.77) * mm, "end": v(-63.77, -26.41) * mm});
            skLineSegment(sketch, "E108.6", {"start": v(-63.77, -26.41) * mm, "end": v(-63.77, 26.41) * mm});
            skLineSegment(sketch, "E108.7", {"start": v(-63.77, 26.41) * mm, "end": v(-26.41, 63.77) * mm});
            skPoint(sketch, "E108.0.midPoint", {"position": v(0, 63.77) * mm});
            skPoint(sketch, "E108.0.midPoint.positionSnap0", {"position": v(0, 55.27) * mm});
            skSolve(sketch);
        }
        {
            var Q0;
            Q0 = qSketchRegion(id + "F33", true);
            extrude(context, id + "F34", {"entities" : qUnion([Q0]), "operationType" : NewBodyOperationType.REMOVE, "oppositeDirection" : true, "depth" : 24.9 * mm});
        }
        {
            var Q0;
            Q0=qCreatedBy(id+"F13.planeOp",FACE);
            var sketch = newSketch(context, id + "F35", { "sketchPlane" : qUnion([Q0])});
            skCircle(sketch, "E109.cCircle", {"center": v(0, 0) * mm, "radius": 63.65 * mm, "construction": true});
            skLineSegment(sketch, "E109.0", {"start": v(63.65, 26.37) * mm, "end": v(63.65, -26.37) * mm});
            skLineSegment(sketch, "E109.1", {"start": v(63.65, -26.37) * mm, "end": v(26.37, -63.65) * mm});
            skLineSegment(sketch, "E109.2", {"start": v(26.37, -63.65) * mm, "end": v(-26.37, -63.65) * mm});
            skLineSegment(sketch, "E109.3", {"start": v(-26.37, -63.65) * mm, "end": v(-63.65, -26.37) * mm});
            skLineSegment(sketch, "E109.4", {"start": v(-63.65, -26.37) * mm, "end": v(-63.65, 26.37) * mm});
            skLineSegment(sketch, "E109.5", {"start": v(-63.65, 26.37) * mm, "end": v(-26.37, 63.65) * mm});
            skLineSegment(sketch, "E109.6", {"start": v(-26.37, 63.65) * mm, "end": v(26.37, 63.65) * mm});
            skLineSegment(sketch, "E109.7", {"start": v(26.37, 63.65) * mm, "end": v(63.65, 26.37) * mm});
            skPoint(sketch, "E109.0.midPoint", {"position": v(63.65, 0) * mm});
            skSolve(sketch);
        }
        {
            var Q0;
            Q0 = qSketchRegion(id + "F35", true);
            extrude(context, id + "F36", {"entities" : qUnion([Q0]), "operationType" : NewBodyOperationType.REMOVE, "oppositeDirection" : true, "depth" : 86.36 * mm});
        }
        {
            var Q0;
            Q0=makeQuery(id+"F15.boolean.opBoolean","INTERSECT",EDGE,{"derivedFrom":[makeQuery(id+"F12.opExtrude","SWEPT_FACE",FACE,{"disambiguationData":[OSD([sQuery(id+"F11.wireOp",EDGE,"E33")])]}),makeQuery(id+"F15.opExtrude","CAP_FACE",FACE,{"disambiguationData":[OSD([sQuery(id+"F14.wireOp",EDGE,"E36.0"),sQuery(id+"F14.wireOp",EDGE,"E36.1"),sQuery(id+"F14.wireOp",EDGE,"E36.2"),sQuery(id+"F14.wireOp",EDGE,"E36.3"),sQuery(id+"F14.wireOp",EDGE,"E36.4"),sQuery(id+"F14.wireOp",EDGE,"E36.5"),sQuery(id+"F14.wireOp",EDGE,"E36.6"),sQuery(id+"F14.wireOp",EDGE,"E36.7"),sQuery(id+"F14.wireOp",EDGE,"E37.0"),sQuery(id+"F14.wireOp",EDGE,"E37.1"),sQuery(id+"F14.wireOp",EDGE,"E37.2"),sQuery(id+"F14.wireOp",EDGE,"E37.3"),sQuery(id+"F14.wireOp",EDGE,"E37.4"),sQuery(id+"F14.wireOp",EDGE,"E37.5"),sQuery(id+"F14.wireOp",EDGE,"E37.6"),sQuery(id+"F14.wireOp",EDGE,"E37.7")])],"isStart":true})]});
            var Q1;
            Q1=makeQuery(id+"F15.boolean.opBoolean","INTERSECT",EDGE,{"derivedFrom":[makeQuery(id+"F12.opExtrude","SWEPT_FACE",FACE,{"disambiguationData":[OSD([sQuery(id+"F11.wireOp",EDGE,"E32")])]}),makeQuery(id+"F15.opExtrude","CAP_FACE",FACE,{"disambiguationData":[OSD([sQuery(id+"F14.wireOp",EDGE,"E36.0"),sQuery(id+"F14.wireOp",EDGE,"E36.1"),sQuery(id+"F14.wireOp",EDGE,"E36.2"),sQuery(id+"F14.wireOp",EDGE,"E36.3"),sQuery(id+"F14.wireOp",EDGE,"E36.4"),sQuery(id+"F14.wireOp",EDGE,"E36.5"),sQuery(id+"F14.wireOp",EDGE,"E36.6"),sQuery(id+"F14.wireOp",EDGE,"E36.7"),sQuery(id+"F14.wireOp",EDGE,"E37.0"),sQuery(id+"F14.wireOp",EDGE,"E37.1"),sQuery(id+"F14.wireOp",EDGE,"E37.2"),sQuery(id+"F14.wireOp",EDGE,"E37.3"),sQuery(id+"F14.wireOp",EDGE,"E37.4"),sQuery(id+"F14.wireOp",EDGE,"E37.5"),sQuery(id+"F14.wireOp",EDGE,"E37.6"),sQuery(id+"F14.wireOp",EDGE,"E37.7")])],"isStart":true})]});
            var Q2;
            Q2=makeQuery(id+"F15.boolean.opBoolean","INTERSECT",EDGE,{"derivedFrom":[makeQuery(id+"F12.opExtrude","SWEPT_FACE",FACE,{"disambiguationData":[OSD([sQuery(id+"F11.wireOp",EDGE,"E34")])]}),makeQuery(id+"F15.opExtrude","CAP_FACE",FACE,{"disambiguationData":[OSD([sQuery(id+"F14.wireOp",EDGE,"E36.0"),sQuery(id+"F14.wireOp",EDGE,"E36.1"),sQuery(id+"F14.wireOp",EDGE,"E36.2"),sQuery(id+"F14.wireOp",EDGE,"E36.3"),sQuery(id+"F14.wireOp",EDGE,"E36.4"),sQuery(id+"F14.wireOp",EDGE,"E36.5"),sQuery(id+"F14.wireOp",EDGE,"E36.6"),sQuery(id+"F14.wireOp",EDGE,"E36.7"),sQuery(id+"F14.wireOp",EDGE,"E37.0"),sQuery(id+"F14.wireOp",EDGE,"E37.1"),sQuery(id+"F14.wireOp",EDGE,"E37.2"),sQuery(id+"F14.wireOp",EDGE,"E37.3"),sQuery(id+"F14.wireOp",EDGE,"E37.4"),sQuery(id+"F14.wireOp",EDGE,"E37.5"),sQuery(id+"F14.wireOp",EDGE,"E37.6"),sQuery(id+"F14.wireOp",EDGE,"E37.7")])],"isStart":true})]});
            var Q3;
            Q3=makeQuery(id+"F15.boolean.opBoolean","INTERSECT",EDGE,{"derivedFrom":[makeQuery(id+"F12.opExtrude","SWEPT_FACE",FACE,{"disambiguationData":[OSD([sQuery(id+"F11.wireOp",EDGE,"E35")])]}),makeQuery(id+"F15.opExtrude","CAP_FACE",FACE,{"disambiguationData":[OSD([sQuery(id+"F14.wireOp",EDGE,"E36.0"),sQuery(id+"F14.wireOp",EDGE,"E36.1"),sQuery(id+"F14.wireOp",EDGE,"E36.2"),sQuery(id+"F14.wireOp",EDGE,"E36.3"),sQuery(id+"F14.wireOp",EDGE,"E36.4"),sQuery(id+"F14.wireOp",EDGE,"E36.5"),sQuery(id+"F14.wireOp",EDGE,"E36.6"),sQuery(id+"F14.wireOp",EDGE,"E36.7"),sQuery(id+"F14.wireOp",EDGE,"E37.0"),sQuery(id+"F14.wireOp",EDGE,"E37.1"),sQuery(id+"F14.wireOp",EDGE,"E37.2"),sQuery(id+"F14.wireOp",EDGE,"E37.3"),sQuery(id+"F14.wireOp",EDGE,"E37.4"),sQuery(id+"F14.wireOp",EDGE,"E37.5"),sQuery(id+"F14.wireOp",EDGE,"E37.6"),sQuery(id+"F14.wireOp",EDGE,"E37.7")])],"isStart":true})]});
            var Q4;
            Q4=makeQuery(id+"F15.boolean.opBoolean","INTERSECT",EDGE,{"derivedFrom":[makeQuery(id+"F12.opExtrude","SWEPT_FACE",FACE,{"disambiguationData":[OSD([sQuery(id+"F11.wireOp",EDGE,"E28")])]}),makeQuery(id+"F15.opExtrude","CAP_FACE",FACE,{"disambiguationData":[OSD([sQuery(id+"F14.wireOp",EDGE,"E36.0"),sQuery(id+"F14.wireOp",EDGE,"E36.1"),sQuery(id+"F14.wireOp",EDGE,"E36.2"),sQuery(id+"F14.wireOp",EDGE,"E36.3"),sQuery(id+"F14.wireOp",EDGE,"E36.4"),sQuery(id+"F14.wireOp",EDGE,"E36.5"),sQuery(id+"F14.wireOp",EDGE,"E36.6"),sQuery(id+"F14.wireOp",EDGE,"E36.7"),sQuery(id+"F14.wireOp",EDGE,"E37.0"),sQuery(id+"F14.wireOp",EDGE,"E37.1"),sQuery(id+"F14.wireOp",EDGE,"E37.2"),sQuery(id+"F14.wireOp",EDGE,"E37.3"),sQuery(id+"F14.wireOp",EDGE,"E37.4"),sQuery(id+"F14.wireOp",EDGE,"E37.5"),sQuery(id+"F14.wireOp",EDGE,"E37.6"),sQuery(id+"F14.wireOp",EDGE,"E37.7")])],"isStart":true})]});
            var Q5;
            Q5=makeQuery(id+"F15.boolean.opBoolean","INTERSECT",EDGE,{"derivedFrom":[makeQuery(id+"F12.opExtrude","SWEPT_FACE",FACE,{"disambiguationData":[OSD([sQuery(id+"F11.wireOp",EDGE,"E29")])]}),makeQuery(id+"F15.opExtrude","CAP_FACE",FACE,{"disambiguationData":[OSD([sQuery(id+"F14.wireOp",EDGE,"E36.0"),sQuery(id+"F14.wireOp",EDGE,"E36.1"),sQuery(id+"F14.wireOp",EDGE,"E36.2"),sQuery(id+"F14.wireOp",EDGE,"E36.3"),sQuery(id+"F14.wireOp",EDGE,"E36.4"),sQuery(id+"F14.wireOp",EDGE,"E36.5"),sQuery(id+"F14.wireOp",EDGE,"E36.6"),sQuery(id+"F14.wireOp",EDGE,"E36.7"),sQuery(id+"F14.wireOp",EDGE,"E37.0"),sQuery(id+"F14.wireOp",EDGE,"E37.1"),sQuery(id+"F14.wireOp",EDGE,"E37.2"),sQuery(id+"F14.wireOp",EDGE,"E37.3"),sQuery(id+"F14.wireOp",EDGE,"E37.4"),sQuery(id+"F14.wireOp",EDGE,"E37.5"),sQuery(id+"F14.wireOp",EDGE,"E37.6"),sQuery(id+"F14.wireOp",EDGE,"E37.7")])],"isStart":true})]});
            var Q6;
            Q6=makeQuery(id+"F15.boolean.opBoolean","INTERSECT",EDGE,{"derivedFrom":[makeQuery(id+"F12.opExtrude","SWEPT_FACE",FACE,{"disambiguationData":[OSD([sQuery(id+"F11.wireOp",EDGE,"E30")])]}),makeQuery(id+"F15.opExtrude","CAP_FACE",FACE,{"disambiguationData":[OSD([sQuery(id+"F14.wireOp",EDGE,"E36.0"),sQuery(id+"F14.wireOp",EDGE,"E36.1"),sQuery(id+"F14.wireOp",EDGE,"E36.2"),sQuery(id+"F14.wireOp",EDGE,"E36.3"),sQuery(id+"F14.wireOp",EDGE,"E36.4"),sQuery(id+"F14.wireOp",EDGE,"E36.5"),sQuery(id+"F14.wireOp",EDGE,"E36.6"),sQuery(id+"F14.wireOp",EDGE,"E36.7"),sQuery(id+"F14.wireOp",EDGE,"E37.0"),sQuery(id+"F14.wireOp",EDGE,"E37.1"),sQuery(id+"F14.wireOp",EDGE,"E37.2"),sQuery(id+"F14.wireOp",EDGE,"E37.3"),sQuery(id+"F14.wireOp",EDGE,"E37.4"),sQuery(id+"F14.wireOp",EDGE,"E37.5"),sQuery(id+"F14.wireOp",EDGE,"E37.6"),sQuery(id+"F14.wireOp",EDGE,"E37.7")])],"isStart":true})]});
            var Q7;
            Q7=makeQuery(id+"F15.boolean.opBoolean","INTERSECT",EDGE,{"derivedFrom":[makeQuery(id+"F12.opExtrude","SWEPT_FACE",FACE,{"disambiguationData":[OSD([sQuery(id+"F11.wireOp",EDGE,"E31")])]}),makeQuery(id+"F15.opExtrude","CAP_FACE",FACE,{"disambiguationData":[OSD([sQuery(id+"F14.wireOp",EDGE,"E36.0"),sQuery(id+"F14.wireOp",EDGE,"E36.1"),sQuery(id+"F14.wireOp",EDGE,"E36.2"),sQuery(id+"F14.wireOp",EDGE,"E36.3"),sQuery(id+"F14.wireOp",EDGE,"E36.4"),sQuery(id+"F14.wireOp",EDGE,"E36.5"),sQuery(id+"F14.wireOp",EDGE,"E36.6"),sQuery(id+"F14.wireOp",EDGE,"E36.7"),sQuery(id+"F14.wireOp",EDGE,"E37.0"),sQuery(id+"F14.wireOp",EDGE,"E37.1"),sQuery(id+"F14.wireOp",EDGE,"E37.2"),sQuery(id+"F14.wireOp",EDGE,"E37.3"),sQuery(id+"F14.wireOp",EDGE,"E37.4"),sQuery(id+"F14.wireOp",EDGE,"E37.5"),sQuery(id+"F14.wireOp",EDGE,"E37.6"),sQuery(id+"F14.wireOp",EDGE,"E37.7")])],"isStart":true})]});
            var Q8;
            Q8=makeQuery(id+"F15.opExtrude","CAP_EDGE",EDGE,{"disambiguationData":[OSD([sQuery(id+"F14.wireOp",EDGE,"E37.4")])],"isStart":true});
            var Q9;
            Q9=makeQuery(id+"F15.opExtrude","CAP_EDGE",EDGE,{"disambiguationData":[OSD([sQuery(id+"F14.wireOp",EDGE,"E37.5")])],"isStart":true});
            var Q10;
            Q10=makeQuery(id+"F15.opExtrude","CAP_EDGE",EDGE,{"disambiguationData":[OSD([sQuery(id+"F14.wireOp",EDGE,"E37.6")])],"isStart":true});
            var Q11;
            Q11=makeQuery(id+"F15.opExtrude","CAP_EDGE",EDGE,{"disambiguationData":[OSD([sQuery(id+"F14.wireOp",EDGE,"E37.7")])],"isStart":true});
            var Q12;
            Q12=makeQuery(id+"F15.opExtrude","CAP_EDGE",EDGE,{"disambiguationData":[OSD([sQuery(id+"F14.wireOp",EDGE,"E37.0")])],"isStart":true});
            var Q13;
            Q13=makeQuery(id+"F15.opExtrude","CAP_EDGE",EDGE,{"disambiguationData":[OSD([sQuery(id+"F14.wireOp",EDGE,"E37.1")])],"isStart":true});
            var Q14;
            Q14=makeQuery(id+"F15.opExtrude","CAP_EDGE",EDGE,{"disambiguationData":[OSD([sQuery(id+"F14.wireOp",EDGE,"E37.2")])],"isStart":true});
            var Q15;
            Q15=makeQuery(id+"F15.opExtrude","CAP_EDGE",EDGE,{"disambiguationData":[OSD([sQuery(id+"F14.wireOp",EDGE,"E37.3")])],"isStart":true});
            var Q16;
            Q16=makeQuery(id+"F19.opExtrude","SWEPT_EDGE",EDGE,{"disambiguationData":[OSD([sQuery(id+"F18.wireOp",EDGE,"E47.top"),sQuery(id+"F18.wireOp",EDGE,"E49")])]});
            var Q17;
            Q17=makeQuery(id+"F17.opExtrude","SWEPT_EDGE",EDGE,{"disambiguationData":[OSD([sQuery(id+"F16.wireOp",EDGE,"E43"),sQuery(id+"F16.wireOp",EDGE,"E44")])]});
            var Q18;
            Q18=makeQuery(id+"F19.opExtrude","SWEPT_EDGE",EDGE,{"disambiguationData":[OSD([sQuery(id+"F18.wireOp",EDGE,"E48"),sQuery(id+"F18.wireOp",EDGE,"E50")])]});
            var Q19;
            Q19=makeQuery(id+"F17.opExtrude","SWEPT_EDGE",EDGE,{"disambiguationData":[OSD([sQuery(id+"F16.wireOp",EDGE,"E40"),sQuery(id+"F16.wireOp",EDGE,"E45")])]});
            chamfer(context, id + "F37", {"entities" : qUnion([Q0, Q1, Q2, Q3, Q4, Q5, Q6, Q7, Q8, Q9, Q10, Q11, Q12, Q13, Q14, Q15, Q16, Q17, Q18, Q19]), "width" : 5.08 * mm, "tangentPropagation" : true});
        }
        {
            var Q0;
            Q0=makeQuery(id+"F20.opExtrude","SWEPT_FACE",FACE,{"disambiguationData":[OSD([sQuery(id+"F16.wireOp",EDGE,"E40")])]});
            var Q1;
            Q1=makeQuery(id+"F20.opExtrude","SWEPT_EDGE",EDGE,{"disambiguationData":[OSD([sQuery(id+"F16.wireOp",EDGE,"E43"),sQuery(id+"F16.wireOp",EDGE,"E44")])]});
            chamfer(context, id + "F38", {"entities" : qUnion([Q0, Q1]), "width" : 5.08 * mm, "tangentPropagation" : true});
        }
        {
            var Q0;
            Q0=qCreatedBy(id+"F5.planeOp",FACE);
            cPlane(context, id + "F39", {"entities" : qUnion([Q0]), "cplaneType" : CPlaneType.OFFSET, "offset" : 42.93 * mm, "width" : 152.4 * mm, "height" : 152.4 * mm});
        }
        {
            var Q0;
            Q0=qCreatedBy(id+"F39.planeOp",FACE);
            var sketch = newSketch(context, id + "F40", { "sketchPlane" : qUnion([Q0])});
            skCircle(sketch, "E110", {"center": v(38.9, -93.93) * mm, "radius": 2.23 * mm});
            skCircle(sketch, "E111", {"center": v(-39.02, -93.93) * mm, "radius": 2.24 * mm});
            skCircle(sketch, "E112", {"center": v(-94.07, -38.95) * mm, "radius": 2.27 * mm});
            skCircle(sketch, "E113", {"center": v(-94.07, 38.9) * mm, "radius": 2.22 * mm});
            skCircle(sketch, "E114", {"center": v(-39.02, 94.12) * mm, "radius": 2.19 * mm});
            skCircle(sketch, "E115", {"center": v(38.9, 94.12) * mm, "radius": 2.2 * mm});
            skCircle(sketch, "E116", {"center": v(93.83, 38.9) * mm, "radius": 2.23 * mm});
            skCircle(sketch, "E117", {"center": v(93.83, -38.95) * mm, "radius": 2.23 * mm});
            skSolve(sketch);
        }
        {
            var Q0;
            Q0 = qSketchRegion(id + "F40", true);
            extrude(context, id + "F41", {"entities" : qUnion([Q0]), "depth" : 4.06 * mm});
        }
        {
            var Q0;
            Q0=qCreatedBy(id+"F39.planeOp",FACE);
            cPlane(context, id + "F42", {"entities" : qUnion([Q0]), "cplaneType" : CPlaneType.OFFSET, "offset" : 3.8 * mm, "width" : 152.4 * mm, "height" : 152.4 * mm});
        }
        {
            var Q0;
            Q0=qCreatedBy(id+"F42.planeOp",FACE);
            var sketch = newSketch(context, id + "F43", { "sketchPlane" : qUnion([Q0])});
            skCircle(sketch, "E118.cCircle", {"center": v(38.89, -94) * mm, "radius": 2.63 * mm, "construction": true});
            skLineSegment(sketch, "E118.0", {"start": v(40.4, -96.62) * mm, "end": v(37.37, -96.62) * mm});
            skLineSegment(sketch, "E118.1", {"start": v(37.37, -96.62) * mm, "end": v(35.85, -94) * mm});
            skLineSegment(sketch, "E118.2", {"start": v(35.85, -94) * mm, "end": v(37.37, -91.37) * mm});
            skLineSegment(sketch, "E118.3", {"start": v(37.37, -91.37) * mm, "end": v(40.4, -91.37) * mm});
            skLineSegment(sketch, "E118.4", {"start": v(40.4, -91.37) * mm, "end": v(41.92, -94) * mm});
            skLineSegment(sketch, "E118.5", {"start": v(41.92, -94) * mm, "end": v(40.4, -96.62) * mm});
            skPoint(sketch, "E118.0.midPoint", {"position": v(38.89, -96.62) * mm});
            skCircle(sketch, "E119.cCircle", {"center": v(-39.13, -94) * mm, "radius": 2.63 * mm, "construction": true});
            skLineSegment(sketch, "E119.0", {"start": v(-37.6, -96.62) * mm, "end": v(-40.64, -96.62) * mm});
            skLineSegment(sketch, "E119.1", {"start": v(-40.64, -96.62) * mm, "end": v(-42.16, -94) * mm});
            skLineSegment(sketch, "E119.2", {"start": v(-42.16, -94) * mm, "end": v(-40.64, -91.37) * mm});
            skLineSegment(sketch, "E119.3", {"start": v(-40.64, -91.37) * mm, "end": v(-37.6, -91.37) * mm});
            skLineSegment(sketch, "E119.4", {"start": v(-37.6, -91.37) * mm, "end": v(-36.1, -94) * mm});
            skLineSegment(sketch, "E119.5", {"start": v(-36.1, -94) * mm, "end": v(-37.6, -96.62) * mm});
            skPoint(sketch, "E119.0.midPoint", {"position": v(-39.13, -96.62) * mm});
            skCircle(sketch, "E120.cCircle", {"center": v(-94.05, -38.93) * mm, "radius": 2.62 * mm, "construction": true});
            skLineSegment(sketch, "E120.0", {"start": v(-94.02, -41.96) * mm, "end": v(-96.66, -40.47) * mm});
            skLineSegment(sketch, "E120.1", {"start": v(-96.66, -40.47) * mm, "end": v(-96.69, -37.44) * mm});
            skLineSegment(sketch, "E120.2", {"start": v(-96.69, -37.44) * mm, "end": v(-94.08, -35.9) * mm});
            skLineSegment(sketch, "E120.3", {"start": v(-94.08, -35.9) * mm, "end": v(-91.44, -37.4) * mm});
            skLineSegment(sketch, "E120.4", {"start": v(-91.44, -37.4) * mm, "end": v(-91.41, -40.42) * mm});
            skLineSegment(sketch, "E120.5", {"start": v(-91.41, -40.42) * mm, "end": v(-94.02, -41.96) * mm});
            skPoint(sketch, "E120.0.midPoint", {"position": v(-95.34, -41.22) * mm});
            skCircle(sketch, "E121.cCircle", {"center": v(-94.05, 39) * mm, "radius": 2.64 * mm, "construction": true});
            skLineSegment(sketch, "E121.0", {"start": v(-96.69, 37.47) * mm, "end": v(-96.69, 40.52) * mm});
            skLineSegment(sketch, "E121.1", {"start": v(-96.69, 40.52) * mm, "end": v(-94.05, 42.04) * mm});
            skLineSegment(sketch, "E121.2", {"start": v(-94.05, 42.04) * mm, "end": v(-91.41, 40.52) * mm});
            skLineSegment(sketch, "E121.3", {"start": v(-91.41, 40.52) * mm, "end": v(-91.41, 37.47) * mm});
            skLineSegment(sketch, "E121.4", {"start": v(-91.41, 37.47) * mm, "end": v(-94.05, 35.95) * mm});
            skLineSegment(sketch, "E121.5", {"start": v(-94.05, 35.95) * mm, "end": v(-96.69, 37.47) * mm});
            skPoint(sketch, "E121.0.midPoint", {"position": v(-96.69, 39) * mm});
            skCircle(sketch, "E122.cCircle", {"center": v(-38.99, 94.19) * mm, "radius": 2.58 * mm, "construction": true});
            skLineSegment(sketch, "E122.0", {"start": v(-37.5, 91.6) * mm, "end": v(-40.48, 91.6) * mm});
            skLineSegment(sketch, "E122.1", {"start": v(-40.48, 91.6) * mm, "end": v(-41.97, 94.19) * mm});
            skLineSegment(sketch, "E122.2", {"start": v(-41.97, 94.19) * mm, "end": v(-40.48, 96.77) * mm});
            skLineSegment(sketch, "E122.3", {"start": v(-40.48, 96.77) * mm, "end": v(-37.5, 96.77) * mm});
            skLineSegment(sketch, "E122.4", {"start": v(-37.5, 96.77) * mm, "end": v(-36, 94.19) * mm});
            skLineSegment(sketch, "E122.5", {"start": v(-36, 94.19) * mm, "end": v(-37.5, 91.6) * mm});
            skPoint(sketch, "E122.0.midPoint", {"position": v(-38.99, 91.6) * mm});
            skCircle(sketch, "E123.cCircle", {"center": v(39.03, 94.19) * mm, "radius": 2.55 * mm, "construction": true});
            skLineSegment(sketch, "E123.0", {"start": v(40.5, 91.64) * mm, "end": v(37.55, 91.64) * mm});
            skLineSegment(sketch, "E123.1", {"start": v(37.55, 91.64) * mm, "end": v(36.08, 94.19) * mm});
            skLineSegment(sketch, "E123.2", {"start": v(36.08, 94.19) * mm, "end": v(37.55, 96.74) * mm});
            skLineSegment(sketch, "E123.3", {"start": v(37.55, 96.74) * mm, "end": v(40.5, 96.74) * mm});
            skLineSegment(sketch, "E123.4", {"start": v(40.5, 96.74) * mm, "end": v(41.97, 94.19) * mm});
            skLineSegment(sketch, "E123.5", {"start": v(41.97, 94.19) * mm, "end": v(40.5, 91.64) * mm});
            skPoint(sketch, "E123.0.midPoint", {"position": v(39.03, 91.64) * mm});
            skCircle(sketch, "E124.cCircle", {"center": v(93.95, 38.94) * mm, "radius": 2.76 * mm, "construction": true});
            skLineSegment(sketch, "E124.0", {"start": v(96.71, 37.34) * mm, "end": v(93.95, 35.74) * mm});
            skLineSegment(sketch, "E124.1", {"start": v(93.95, 35.74) * mm, "end": v(91.18, 37.34) * mm});
            skLineSegment(sketch, "E124.2", {"start": v(91.18, 37.34) * mm, "end": v(91.18, 40.53) * mm});
            skLineSegment(sketch, "E124.3", {"start": v(91.18, 40.53) * mm, "end": v(93.95, 42.13) * mm});
            skLineSegment(sketch, "E124.4", {"start": v(93.95, 42.13) * mm, "end": v(96.71, 40.53) * mm});
            skLineSegment(sketch, "E124.5", {"start": v(96.71, 40.53) * mm, "end": v(96.71, 37.34) * mm});
            skPoint(sketch, "E124.0.midPoint", {"position": v(95.33, 36.54) * mm});
            skCircle(sketch, "E125.cCircle", {"center": v(93.95, -38.93) * mm, "radius": 2.68 * mm, "construction": true});
            skLineSegment(sketch, "E125.0", {"start": v(96.63, -40.48) * mm, "end": v(93.95, -42.03) * mm});
            skLineSegment(sketch, "E125.1", {"start": v(93.95, -42.03) * mm, "end": v(91.26, -40.48) * mm});
            skLineSegment(sketch, "E125.2", {"start": v(91.26, -40.48) * mm, "end": v(91.26, -37.38) * mm});
            skLineSegment(sketch, "E125.3", {"start": v(91.26, -37.38) * mm, "end": v(93.95, -35.84) * mm});
            skLineSegment(sketch, "E125.4", {"start": v(93.95, -35.84) * mm, "end": v(96.63, -37.38) * mm});
            skLineSegment(sketch, "E125.5", {"start": v(96.63, -37.38) * mm, "end": v(96.63, -40.48) * mm});
            skPoint(sketch, "E125.0.midPoint", {"position": v(95.29, -41.26) * mm});
            skSolve(sketch);
        }
        {
            var Q0;
            Q0 = qSketchRegion(id + "F43", true);
            extrude(context, id + "F44", {"entities" : qUnion([Q0]), "depth" : 4.83 * mm});
        }
    });
